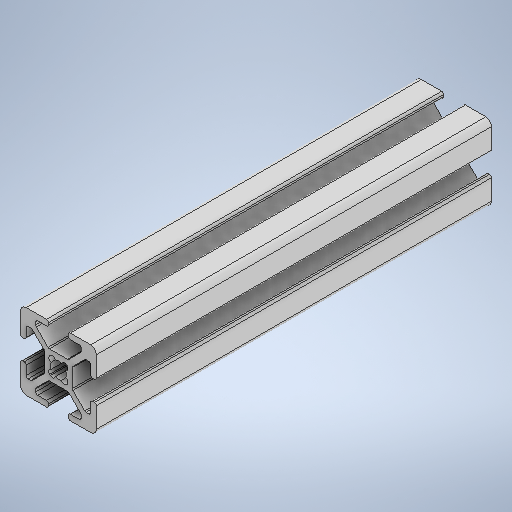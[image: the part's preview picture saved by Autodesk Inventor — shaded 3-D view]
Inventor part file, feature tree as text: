
AUTODESK INVENTOR PART (.ipt)
format: ipt  version: 2025 (Build 290162000, 162)  size: 379,392 bytes
history: native  units: mm
features: extrude x1, sketch x1
ambient origin geometry x8: Origin, YZ Plane, XZ Plane, XY Plane, X Axis, Y Axis, Z Axis, Center Point
bodies: Solid1 (feature_tree)
feature tree (2):
  extrude  "Extrusion1"  Depth=104.025mm
  sketch  "Sketch1"  dims[d0=104.025mm d1=0.0mm d2=1.0mm d3=1.0mm d4=1.0mm d5=0.15mm d6=0.25mm d7=0.375mm d8=14.3117mm d9=0.75mm d10=20.594885mm d11=0.0625mm d12=0.75mm d13=0.375mm]
